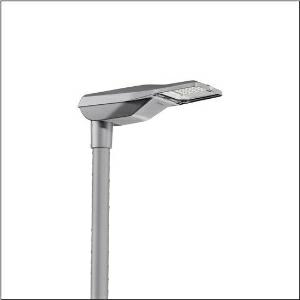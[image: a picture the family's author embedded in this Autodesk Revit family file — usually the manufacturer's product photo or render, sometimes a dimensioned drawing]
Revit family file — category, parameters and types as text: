
# Revit family: streetlight_sl_21_iq_micro___st0_8a_5xe1c21d08cb_82e6
name_source: partatom
category: Lighting Fixtures
units: mm (PartAtom-declared; Revit-internal decimal feet)

## family parameters
Cut with Voids When Loaded = No
Host = Face
Light Source = No
Part Type = Normal
Room Calculation Point = No
Round Connector Dimension = Use Diameter
Shared = No

## types (1)
- --- (1 x LED, 2380 lm, 19.4 W, 2200K)
    Apparent Load = 19 VA
    CIE Flux Codes = 38 75 97 100 100
    Color Rendering = 70
    Color Temperature = 2200K
    Default Elevation = 1800 mm
    Description = Streetlight SL 21 iQ micro, mast luminaire, primary light control with lens, of PMMA, primary optical cover: cover, of toughened safety glass, transparent, light distribution: ST0.8a, light emission: direct distribution, primary light characteristic: asymmetric, installation type: post-top, side-entry, LED, High Power LED, rated luminous flux: 2.380lm, luminous efficacy: 123lm/W, light colour: 722, colour temperature: 2200K, control gear: iQ-Comfort, control: Auto-Match, Temp-Guard, Lumen-Switch, Night-Set, Smart-Wire, Light-Fading, Desk-Remote (wireless, voltage-free reading and setting of iQ features in the workshop via application-optimized NFC function/RFID function), optimised constant luminous flux control (CLO 2.0), pre-setting: linear dimming characteristic, mains connection: 220..240V, AC, 50/60Hz, start of lifetime: 19W, end of service life: 20W, reduction: 10W, luminaire housing, of diecast aluminium, powder-coated, Siteco® metallic grey (DB 702S), corrosivity category C5 mid according to DIN EN ISO 12944, please order mast flange separately, inclination adjustable: 0°, 5°, 10°, 15°, sealing non-destructively replaceable, multi-level sealing system, length: 528mm, width: 235mm, height: 110mm, mast flange for spigot size: 42mm (side-entry): 5XC10008XM4, 60/48mm (side-entry/post-top): 5XC10108XM2, 76/60mm (side-entry/post-top): 5XC10108XM1, protection rating (complete): IP66, insulation class (complete): insulation class II (safety insulation), certification: CE, ENEC, ENEC+, VDE, impact resistance: IK10, permissible operating ambient temperature for outdoor applications: -40..+50°C, standard-compliant lighting for roads and squares, packaging unit: 1 piece

Light Distribution: ST0.8a
    Height = 110 mm
    Lamp = 1 x LED
    Lamp Light Flux = 2380 lm
    Lamp Power = 19.4 W
    Lamp count = 1
    Length = 528 mm
    Luminous efficacy = 123 lm/W
    Manufacturer = Siteco
    ModVariant = No
    Model = 5XE1C21D08CB
    Number of Poles = 1
    OnlyDefault = Yes
    Power Factor = 1
    Product Name = Streetlight SL 21 iQ micro | ST0.8a
    Product group = mast luminaire | pylon top
    ProductGroupID = 6100
    Protection Class = Protection class II
    Protection Degree = IP 66
    RLX_Detail_Level = 1
    RLX_Emergency_Light_Flux = 0 lm
    RLX_Emergency_Type = 0
    RLX_Emergency_Type_DB = No
    RlxData = <blob elided: 98733 chars, md5=1013b9e7>
    Socket = socket
    Standby Power = 0 W
    System Light Flux = 2380 lm
    System Power = 19 W
    Type Comments = factory setting: luminous flux: 100 % | dim-lin: 254 | 387 mA
    Type Image = l_1006881.jpg
    URL = http://relux.com
    VarID = @adj_138536
    Voltage = 0 V
    Weight = 0.00 kg
    Width = 235 mm

## geometry (parser evidence)
native form markers: Blend x4, Sweep x10
no freeform markers — native parametric forms only
